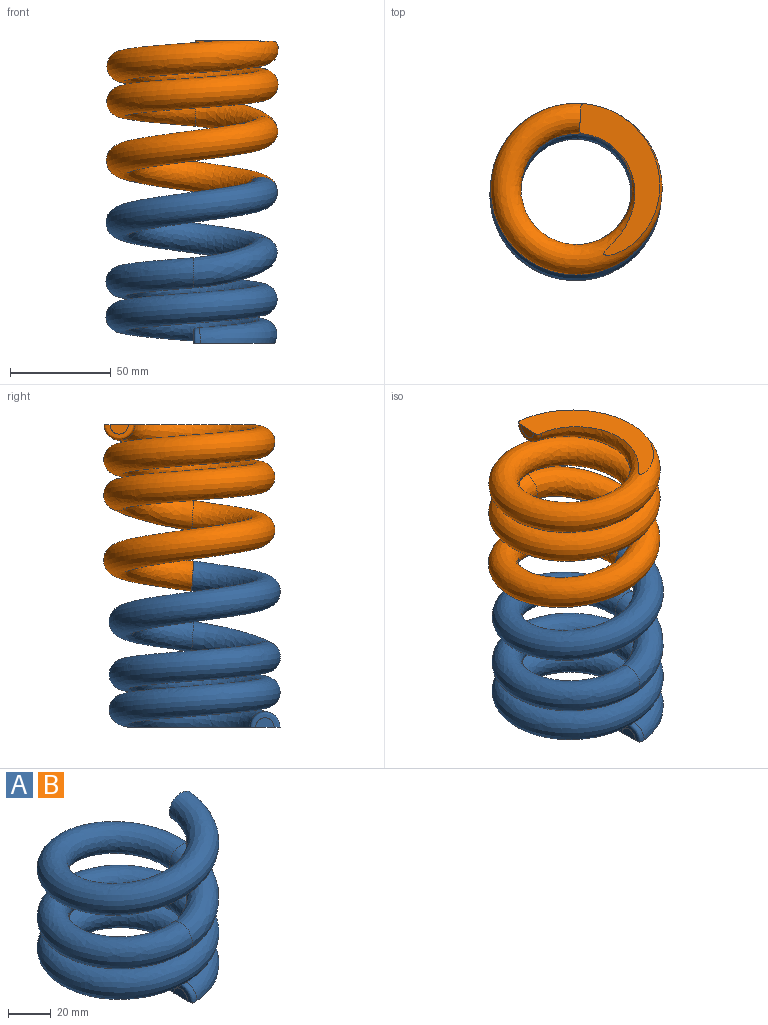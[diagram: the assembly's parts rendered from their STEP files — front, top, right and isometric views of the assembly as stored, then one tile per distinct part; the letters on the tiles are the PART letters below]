
ASSEMBLY  parts=2 mates=1
PART A: 7 faces, bbox 111.8x116.6x103.9 mm
  f0: plane 9.1x4.74mm, normal (-1,0,0), area 34mm2, adj f5,f6
  f1: bspline ~84.87x84.8mm, area 19675.9mm2, adj f2,f5,f6
  f2: bspline ~51.74x51.3mm, area 2628.8mm2, adj f1,f4
  f3: plane 17.08x17.05mm, normal (0.04,1,0.07), area 176.7mm2, adj f4
  f4: bspline ~108.81x103.94mm, area 10446.3mm2, adj f2,f3
  f5: plane 82.37x48.99mm, normal (0,0,-1), area 1109.4mm2, adj f0,f1,f6
  f6: bspline ~15.41x9.12mm, area 106.6mm2, adj f0,f1,f5
PART B: same geometry as A
PLACE A rot(axis=(0,0.04,1),1.6deg) t=(0.06,-0.95,40.04)mm
PLACE B rot(axis=(1,-0.03,0),180deg) t=(0.31,1.75,100.21)mm
MATE fastened B.f3 <-> A.f3  axis (-0.01,-1,-0.07) through (35.08,0,70)mm
